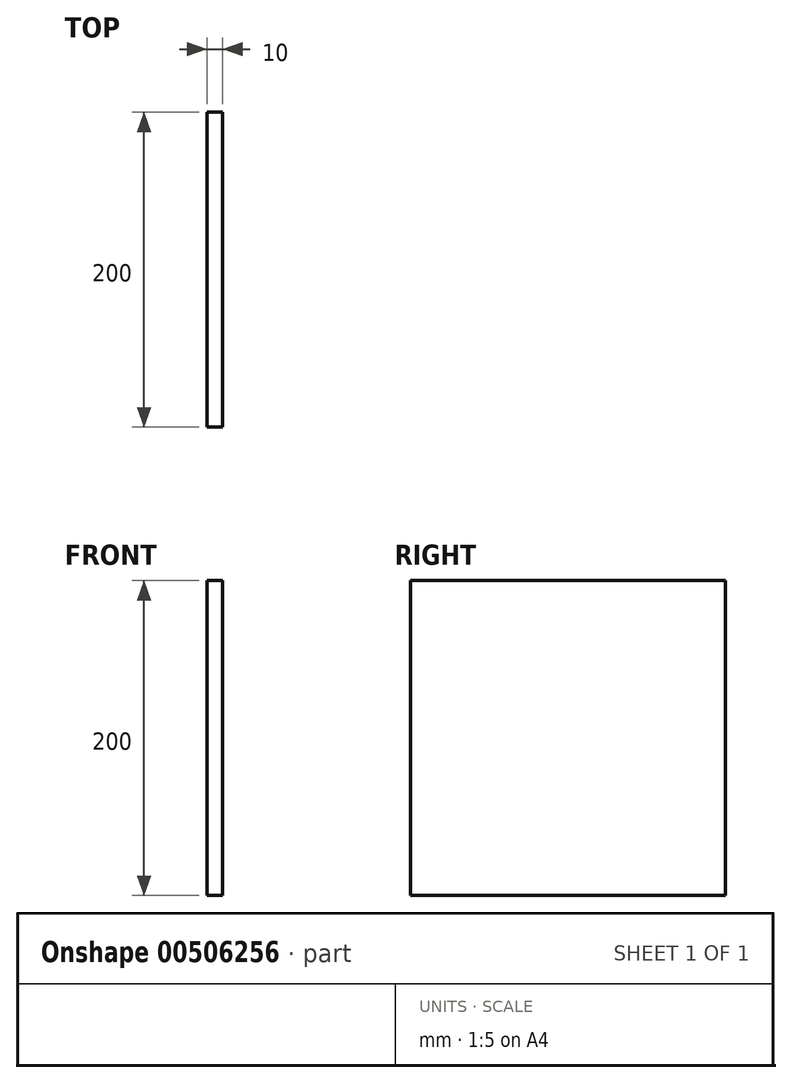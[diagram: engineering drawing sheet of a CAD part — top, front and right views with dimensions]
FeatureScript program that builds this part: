
annotation { "Feature Type Name" : "Feature", "Feature Type Description" : "" }
export const myFeature = defineFeature(function(context is Context, id is Id, definition is map)
    precondition{}
    {
        {
            var Q0;
            Q0=qCreatedBy(makeId("Right.planeOp"),FACE);
            var sketch = newSketch(context, id + "F0", { "sketchPlane" : qUnion([Q0])});
            skLineSegment(sketch, "E0.bottom", {"start": v(0, 0) * mm, "end": v(200, 0) * mm});
            skLineSegment(sketch, "E0.top", {"start": v(0, 200) * mm, "end": v(200, 200) * mm});
            skLineSegment(sketch, "E0.left", {"start": v(0, 0) * mm, "end": v(0, 200) * mm});
            skLineSegment(sketch, "E0.right", {"start": v(200, 0) * mm, "end": v(200, 200) * mm});
            skSolve(sketch);
        }
        {
            var Q0;
            Q0=makeQuery(id+"F0.imprint","IMPRINT",FACE,{"disambiguationData":[TD([[makeQuery(id+"F0.imprint","IMPRINT",EDGE,{"derivedFrom":sQuery(id+"F0.wireOp",EDGE,"E0.bottom")}),1.0]])]});
            extrude(context, id + "F1", {"entities" : qUnion([Q0]), "depth" : 10 * mm});
        }
    });
